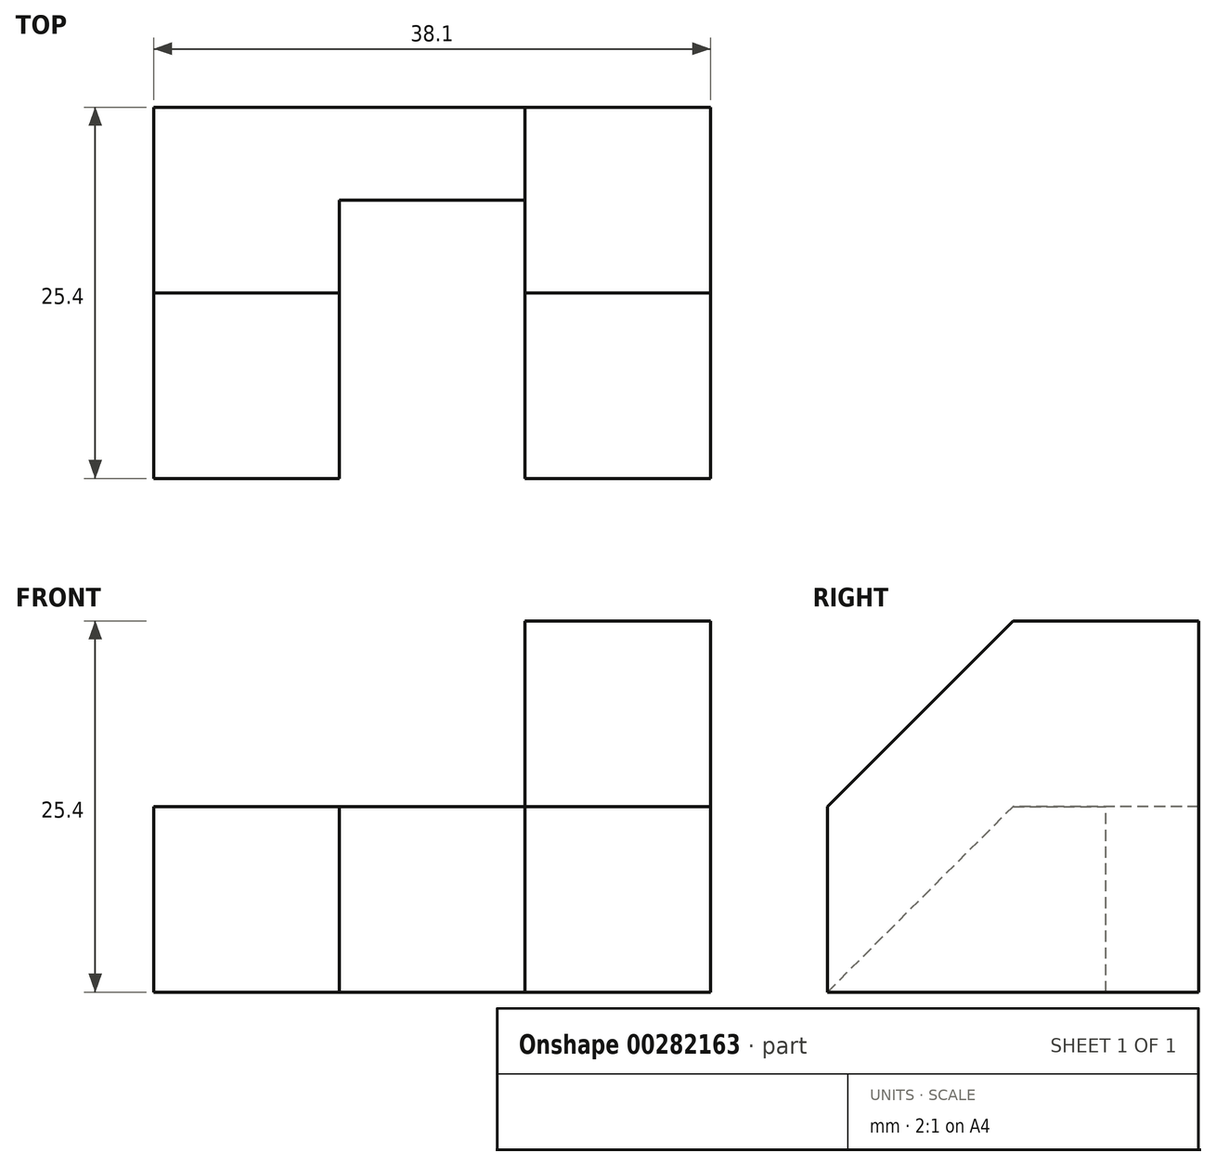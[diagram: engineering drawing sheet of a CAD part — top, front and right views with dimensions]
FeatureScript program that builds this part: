
annotation { "Feature Type Name" : "Feature", "Feature Type Description" : "" }
export const myFeature = defineFeature(function(context is Context, id is Id, definition is map)
    precondition{}
    {
        {
            var Q0;
            Q0=qCreatedBy(makeId("Right.planeOp"),FACE);
            var sketch = newSketch(context, id + "F0", { "sketchPlane" : qUnion([Q0])});
            skLineSegment(sketch, "E0.bottom", {"start": v(0, 0) * mm, "end": v(25.4, 0) * mm});
            skLineSegment(sketch, "E0.top", {"start": v(0, 25.4) * mm, "end": v(25.4, 25.4) * mm});
            skLineSegment(sketch, "E0.left", {"start": v(0, 0) * mm, "end": v(0, 25.4) * mm});
            skLineSegment(sketch, "E0.right", {"start": v(25.4, 0) * mm, "end": v(25.4, 25.4) * mm});
            skSolve(sketch);
        }
        {
            var Q0;
            Q0=makeQuery(id+"F0.imprint","IMPRINT",FACE,{"disambiguationData":[TD([[makeQuery(id+"F0.imprint","IMPRINT",EDGE,{"derivedFrom":sQuery(id+"F0.wireOp",EDGE,"E0.bottom")}),1.0]])]});
            extrude(context, id + "F1", {"entities" : qUnion([Q0]), "depth" : 12.7 * mm});
        }
        {
            var Q0;
            Q0=makeQuery(id+"F1.opExtrude","CAP_FACE",FACE,{"disambiguationData":[OSD([sQuery(id+"F0.wireOp",EDGE,"E0.bottom"),sQuery(id+"F0.wireOp",EDGE,"E0.top"),sQuery(id+"F0.wireOp",EDGE,"E0.left"),sQuery(id+"F0.wireOp",EDGE,"E0.right")])],"isStart":false});
            var sketch = newSketch(context, id + "F2", { "sketchPlane" : qUnion([Q0])});
            skLineSegment(sketch, "E1", {"start": v(0, 25.4) * mm, "end": v(12.7, 25.4) * mm});
            skLineSegment(sketch, "E2", {"start": v(12.7, 25.4) * mm, "end": v(0, 12.7) * mm});
            skLineSegment(sketch, "E3", {"start": v(0, 12.7) * mm, "end": v(0, 25.4) * mm});
            skSolve(sketch);
        }
        {
            var Q0;
            Q0=makeQuery(id+"F2.imprint","IMPRINT",FACE,{"disambiguationData":[TD([[makeQuery(id+"F2.imprint","IMPRINT",EDGE,{"derivedFrom":sQuery(id+"F2.wireOp",EDGE,"E1")}),-1.0]])]});
            extrude(context, id + "F3", {"entities" : qUnion([Q0]), "operationType" : NewBodyOperationType.REMOVE, "oppositeDirection" : true, "depth" : 12.7 * mm});
        }
        {
            var Q0;
            Q0=makeQuery(id+"F1.opExtrude","CAP_FACE",FACE,{"disambiguationData":[OSD([sQuery(id+"F0.wireOp",EDGE,"E0.bottom"),sQuery(id+"F0.wireOp",EDGE,"E0.top"),sQuery(id+"F0.wireOp",EDGE,"E0.left"),sQuery(id+"F0.wireOp",EDGE,"E0.right")])],"isStart":true});
            var sketch = newSketch(context, id + "F4", { "sketchPlane" : qUnion([Q0])});
            skLineSegment(sketch, "E4.bottom", {"start": v(-25.4, 0) * mm, "end": v(0, 0) * mm});
            skLineSegment(sketch, "E4.top", {"start": v(-25.4, 12.7) * mm, "end": v(0, 12.7) * mm});
            skLineSegment(sketch, "E4.left", {"start": v(-25.4, 0) * mm, "end": v(-25.4, 12.7) * mm});
            skLineSegment(sketch, "E4.right", {"start": v(0, 0) * mm, "end": v(0, 12.7) * mm});
            skSolve(sketch);
        }
        {
            var Q0;
            Q0=makeQuery(id+"F4.imprint","IMPRINT",FACE,{"disambiguationData":[TD([[makeQuery(id+"F4.imprint","IMPRINT",EDGE,{"derivedFrom":sQuery(id+"F4.wireOp",EDGE,"E4.bottom")}),-1.0]])]});
            extrude(context, id + "F5", {"entities" : qUnion([Q0]), "operationType" : NewBodyOperationType.ADD, "depth" : 25.4 * mm});
        }
        {
            var Q0;
            Q0=makeQuery(id+"F5.opExtrude","SWEPT_FACE",FACE,{"disambiguationData":[OSD([sQuery(id+"F4.wireOp",EDGE,"E4.top")])]});
            var sketch = newSketch(context, id + "F6", { "sketchPlane" : qUnion([Q0])});
            skLineSegment(sketch, "E5.bottom", {"start": v(0, 0) * mm, "end": v(-12.7, 0) * mm});
            skLineSegment(sketch, "E5.top", {"start": v(0, 19.05) * mm, "end": v(-12.7, 19.05) * mm});
            skLineSegment(sketch, "E5.left", {"start": v(0, 0) * mm, "end": v(0, 19.05) * mm});
            skLineSegment(sketch, "E5.right", {"start": v(-12.7, 0) * mm, "end": v(-12.7, 19.05) * mm});
            skSolve(sketch);
        }
        {
            var Q0;
            Q0=makeQuery(id+"F6.imprint","IMPRINT",FACE,{"disambiguationData":[TD([[makeQuery(id+"F6.imprint","IMPRINT",EDGE,{"derivedFrom":sQuery(id+"F6.wireOp",EDGE,"E5.bottom")}),1.0]])]});
            extrude(context, id + "F7", {"entities" : qUnion([Q0]), "operationType" : NewBodyOperationType.REMOVE, "oppositeDirection" : true, "depth" : 12.7 * mm});
        }
        {
            var Q0;
            Q0=makeQuery(id+"F7.boolean.opBoolean","COPY",FACE,{"derivedFrom":makeQuery(id+"F7.opExtrude","SWEPT_FACE",FACE,{"disambiguationData":[OSD([sQuery(id+"F6.wireOp",EDGE,"E5.right")])]})});
            var sketch = newSketch(context, id + "F8", { "sketchPlane" : qUnion([Q0])});
            skLineSegment(sketch, "E6", {"start": v(0, 12.7) * mm, "end": v(0, 0) * mm});
            skLineSegment(sketch, "E7", {"start": v(0, 0) * mm, "end": v(12.7, 12.7) * mm});
            skLineSegment(sketch, "E8", {"start": v(12.7, 12.7) * mm, "end": v(0, 12.7) * mm});
            skSolve(sketch);
        }
        {
            var Q0;
            Q0=makeQuery(id+"F8.imprint","IMPRINT",FACE,{"disambiguationData":[TD([[makeQuery(id+"F8.imprint","IMPRINT",EDGE,{"derivedFrom":sQuery(id+"F8.wireOp",EDGE,"E6")}),-1.0]])]});
            extrude(context, id + "F9", {"entities" : qUnion([Q0]), "operationType" : NewBodyOperationType.REMOVE, "oppositeDirection" : true, "depth" : 12.7 * mm});
        }
    });
